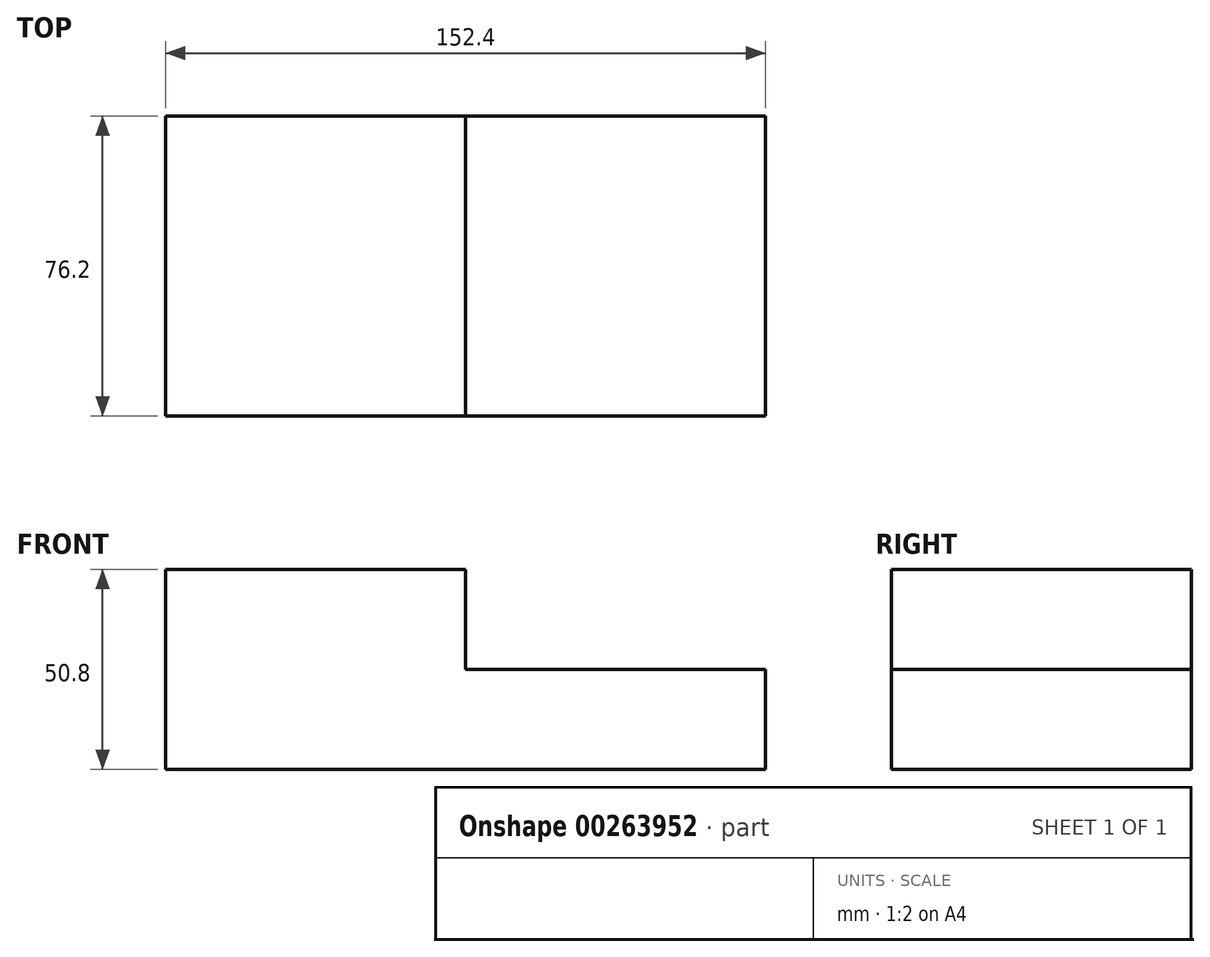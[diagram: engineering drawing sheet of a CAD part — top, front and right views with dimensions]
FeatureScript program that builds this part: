
annotation { "Feature Type Name" : "Feature", "Feature Type Description" : "" }
export const myFeature = defineFeature(function(context is Context, id is Id, definition is map)
    precondition{}
    {
        {
            var Q0;
            Q0=qCreatedBy(makeId("Front.planeOp"),FACE);
            var sketch = newSketch(context, id + "F0", { "sketchPlane" : qUnion([Q0])});
            skLineSegment(sketch, "E0.bottom", {"start": v(-152.4, 0) * mm, "end": v(-76.2, 0) * mm});
            skLineSegment(sketch, "E0.top", {"start": v(-152.4, -50.8) * mm, "end": v(0, -50.8) * mm});
            skLineSegment(sketch, "E0.left", {"start": v(-152.4, 0) * mm, "end": v(-152.4, -50.8) * mm});
            skLineSegment(sketch, "E0.right", {"start": v(0, -25.4) * mm, "end": v(0, -50.8) * mm});
            skLineSegment(sketch, "E1", {"start": v(-76.2, 0) * mm, "end": v(-76.2, -25.4) * mm});
            skLineSegment(sketch, "E2", {"start": v(0, -25.4) * mm, "end": v(-76.2, -25.4) * mm});
            skPoint(sketch, "E3.orphan", {"position": v(0, 0) * mm});
            skPoint(sketch, "E4.orphan", {"position": v(-76.2, -50.8) * mm});
            skSolve(sketch);
        }
        {
            var Q0;
            Q0=makeQuery(id+"F0.imprint","IMPRINT",FACE,{"disambiguationData":[TD([[makeQuery(id+"F0.imprint","IMPRINT",EDGE,{"derivedFrom":sQuery(id+"F0.wireOp",EDGE,"E0.bottom")}),-1.0]])]});
            extrude(context, id + "F1", {"entities" : qUnion([Q0]), "depth" : 76.2 * mm});
        }
    });
